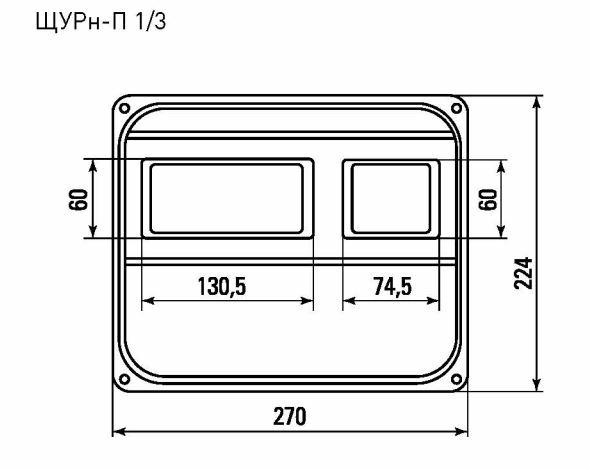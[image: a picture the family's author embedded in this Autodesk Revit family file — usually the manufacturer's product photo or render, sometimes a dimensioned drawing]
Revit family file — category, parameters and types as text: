
# Revit family: EKF_EE_ЩУРн_IP31_PROxima
name_source: partatom
category: Электрооборудование
units: mm (PartAtom-declared; Revit-internal decimal feet)

## family parameters
Всегда вертикально = Да
На основе рабочей плоскости = Нет
Общий = Нет
При загрузке вырезать с полостями = Нет
Размер круглого соединителя = Использовать диаметр
Тип детали = Силовой щит
Точка расчета площади = Да

## types (20) — shared parameters
ADSK_Единица измерения = компл.
ADSK_Завод-изготовитель = EKF
ADSK_Классификация нагрузок = Прочее
ADSK_Количество = 1
ADSK_Количество фаз = 3
ADSK_Коэффициент мощности = 1
ADSK_Материал = RAL 7035_Сталь
ADSK_Напряжение = 400 В
ADSK_Номинальная мощность = 0 Вт
ADSK_Полная мощность = 0 В·А
ADSK_Ток = 125 А
Изготовитель = EKF
Количество DIN-реек = 1
Серия номенклатуры = PROxima
Степень защиты IP = IP31
ТВ = EKF
Тип установки = Навесной
zero-valued in all types: Максимальное количество модулей

## per-type parameters (varying)
| type | ADSK_Код изделия | ADSK_Марка | ADSK_Масса | ADSK_Наименование | ADSK_Обозначение | ADSK_Размер_Высота | ADSK_Размер_Глубина | ADSK_Размер_Ширина | Количество модулей на DIN-рейке | Описание | Тип |
| ЩУРн 1/9 (400х300х140) IP31 EKF PROxima | mb23-1/9 | ЩУРн 1/9 IP31 | 4.38 | Щит учетно-распред. навесной ЩУРн 1/9 (400х300х140) IP31 EKF PROxima | ЩУРн 1/9 IP31 | 400 мм | 140 мм | 300 мм | 9 | Щит учетно-распред. навесной ЩУРн 1/9 (400х300х140) IP31 EKF PROxima | 17 мм |
| ЩУРн 1/12 (400x300x140) IP31 EKF PROxima | mb23-1/12 | ЩУРн 1/12 IP31 | 4.38 | Щит учетно-распред. навесной ЩУРн 1/12 (400x300x140) IP31 EKF PROxima | ЩУРн 1/12 IP31 | 400 мм | 140 мм | 300 мм | 12 | Щит учетно-распред. навесной ЩУРн 1/12 (400x300x140) IP31 EKF PROxima | 19 мм |
| ЩУРн 1/12 с шинами (400x300x140) IP31 EKF PROxima | mb23-1/12sh | ЩУРн 1/12 с шинами IP31 | 4.38 | Щит учетно-распред. навесной ЩУРн 1/12 с шинами (400x300x140) IP31 EKF PROxima | ЩУРн 1/12 с шинами IP31 | 400 мм | 140 мм | 300 мм | 12 | Щит учетно-распред. навесной ЩУРн 1/12 с шинами (400x300x140) IP31 EKF PROxima | 20 мм |
| ЩУРн 1/15 (400x360x140) IP31 EKF PROxima | mb23-1/15 | ЩУРн 1/15 IP31 | 5.6 | Щит учетно-распред. навесной ЩУРн 1/15 (400x360x140) IP31 EKF PROxima | ЩУРн 1/15 IP31 | 400 мм | 140 мм | 360 мм | 15 | Щит учетно-распред. навесной ЩУРн 1/15 (400x360x140) IP31 EKF PROxima | 21 мм |
| ЩУРн 3/12 (500х300х160) IP31 EKF PROxima | mb23-3/12 | ЩУРн 3/12 IP31 | 5.88 | Щит учетно-распред. навесной ЩУРн 3/12 (500х300х160) IP31 EKF PROxima | ЩУРн 3/12 IP31 | 500 мм | 160 мм | 300 мм | 12 | Щит учетно-распред. навесной ЩУРн 3/12 (500х300х160) IP31 EKF PROxima | 23 мм |
| ЩУРн 3/12 (Э) (500х300х120) IP31 EKF PROxima | mb23-3/12e | ЩУРн 3/12 (Э) IP31 | 5 | Щит учетно-распред. навесной счетчик на дин-рейку ЩУРн 3/12 (Э) (500х300х120) IP31 EKF PROxima | ЩУРн 3/12 (Э) IP31 | 500 мм | 120 мм | 300 мм | 12 | Щит учетно-распред. навесной счетчик на дин-рейку ЩУРн 3/12 (Э) (500х300х120) IP31 EKF PROxima | 24 мм |
| ЩУРн 3/18 (500х400х160) IP31 EKF PROxima | mb23-3/18 | ЩУРн 3/18 IP31 | 7 | Щит учетно-распред. навесной ЩУРн 3/18 (500х400х160) IP31 EKF PROxima | ЩУРн 3/18 IP31 | 500 мм | 160 мм | 400 мм | 18 | Щит учетно-распред. навесной ЩУРн 3/18 (500х400х160) IP31 EKF PROxima | 25 мм |
| ЩУРн 3/18 (Э) (500х340х120) IP31 EKF PROxima | mb23-3/18e | ЩУРн 3/18 (Э) IP31 | 5.2 | Щит учетно-распред. навесной счетчик на дин-рейку ЩУРн 3/18 (Э) (500х340х120) IP31 EKF PROxima | ЩУРн 3/18 (Э) IP31 | 500 мм | 120 мм | 340 мм | 18 | Щит учетно-распред. навесной счетчик на дин-рейку ЩУРн 3/18 (Э) (500х340х120) IP31 EKF PROxima | 26 мм |
| ЩУРн 3/24 (500х400х160) IP31 EKF PROxima | mb23-3/24 | ЩУРн 3/24 IP31 | 7.5 | Щит учетно-распред. навесной ЩУРн 3/24 (500х400х160) IP31 EKF PROxima | ЩУРн 3/24 IP31 | 500 мм | 160 мм | 400 мм | 24 | Щит учетно-распред. навесной ЩУРн 3/24 (500х400х160) IP31 EKF PROxima | 28 мм |
| ЩУРн 3/24 (Э) (500х400х120) IP31 EKF PROxima | mb23-3/24e | ЩУРн 3/24 (Э) IP31 | 5.4 | Щит учетно-распред. навесной счетчик на дин-рейку ЩУРн 3/24 (Э) (500х400х120) IP31 EKF PROxima | ЩУРн 3/24 (Э) IP31 | 500 мм | 120 мм | 400 мм | 24 | Щит учетно-распред. навесной счетчик на дин-рейку ЩУРн 3/24 (Э) (500х400х120) IP31 EKF PROxima | 29 мм |
| ЩУРн 3/30 (500х400х160) IP31 EKF PROxima | mb23-3/30-1 | ЩУРн 3/30 IP31 | 7.5 | Щит учетно-распред. навесной ЩУРн 3/30 (500х400х160) IP31 EKF PROxima | ЩУРн 3/30 IP31 | 500 мм | 160 мм | 400 мм | 30 | Щит учетно-распред. навесной ЩУРн 3/30 (500х400х160) IP31 EKF PROxima | 30 мм |
| ЩУРн 3/30 двухдверный (580х490х165) IP31 EKF PROxima | mb23-3/30-2 | ЩУРн 3/30 двухдверный IP31 | 10.75 | Щит учетно-распред. навесной ЩУРн 3/30 двухдверный (580х490х165) IP31 EKF PROxima | ЩУРн 3/30 двухдверный IP31 | 580 мм | 165 мм | 490 мм | 30 | Щит учетно-распред. навесной ЩУРн 3/30 двухдверный (580х490х165) IP31 EKF PROxima | 31 мм |
| ЩУРн 3/36 (560x550x165) IP31 EKF PROxima | mb23-3/36 | ЩУРн 3/36 IP31 | 9.8 | Щит учетно-распред. навесной ЩУРн 3/36 (560x550x165) IP31 EKF PROxima | ЩУРн 3/36 IP31 | 560 мм | 165 мм | 550 мм | 36 | Щит учетно-распред. навесной ЩУРн 3/36 (560x550x165) IP31 EKF PROxima | 32 мм |
| ЩУРн 3/48 (630х400х160) IP31 EKF PROxima | mb23-3/48 | ЩУРн 3/48 IP31 | 9.33 | Щит учетно-распред. навесной ЩУРн 3/48 (630х400х160) IP31 EKF PROxima | ЩУРн 3/48 IP31 | 630 мм | 160 мм | 400 мм | 48 | Щит учетно-распред. навесной ЩУРн 3/48 (630х400х160) IP31 EKF PROxima | 33 мм |
| ЩУРн 3/48 двухдверный (580х620х165) IP31 EKF PROxima | mb23-3/48-2 | ЩУРн 3/48 двухдверный IP31 | 13.12 | Щит учетно-распред. навесной ЩУРн 3/48 двухдверный (580х620х165) IP31 EKF PROxima | ЩУРн 3/48 двухдверный IP31 | 580 мм | 165 мм | 620 мм | 48 | Щит учетно-распред. навесной ЩУРн 3/48 двухдверный (580х620х165) IP31 EKF PROxima | 34 мм |
| ЩУРн 3/9 (500х300х160) IP31 EKF PROxima | mb23-3/9 | ЩУРн 3/9 IP31 | 5.88 | Щит учетно-распред. навесной ЩУРн 3/9 (500х300х160) IP31 EKF PROxima | ЩУРн 3/9 IP31 | 500 мм | 160 мм | 300 мм | 9 | Щит учетно-распред. навесной ЩУРн 3/9 (500х300х160) IP31 EKF PROxima | 35 мм |
| ЩУРн 3/9 (Э) (500х300х120) IP31 EKF PROxima | mb23-3/9e | ЩУРн 3/9 (Э) IP31 | 5 | Щит учетно-распред. навесной счетчик на дин-рейку ЩУРн 3/9 (Э) (500х300х120) IP31 EKF PROxima | ЩУРн 3/9 (Э) IP31 | 500 мм | 120 мм | 300 мм | 9 | Щит учетно-распред. навесной счетчик на дин-рейку ЩУРн 3/9 (Э) (500х300х120) IP31 EKF PROxima | 36 мм |
| ЩУРн 1/9 (Э) (360x280x110) IP31 EKF PROxima | mb23-1/9e | ЩУРн 1/9 (Э) IP31 | 3.5 | Щит учетно-распред. навесной счетчик на дин-рейку ЩУРн 1/9 (Э) (360x280x110) IP31 EKF PROxima | ЩУРн 1/9 (Э) IP31 | 360 мм | 110 мм | 280 мм | 9 | Щит учетно-распред. навесной счетчик на дин-рейку ЩУРн 1/9 (Э) (360x280x110) IP31 EKF PROxima | 38 мм |
| ЩУРн 1/12 (Э) (360х280х110) IP31 EKF PROxima | mb23-1/12e | ЩУРн 1/12 (Э) IP31 | 3.5 | Щит учетно-распред. навесной счетчик на дин-рейку ЩУРн 1/12 (Э) (360х280х110) IP31 EKF PROxima | ЩУРн 1/12 (Э) IP31 | 360 мм | 110 мм | 280 мм | 12 | Щит учетно-распред. навесной счетчик на дин-рейку ЩУРн 1/12 (Э) (360х280х110) IP31 EKF PROxima | 40 мм |
| ЩУРн- 1/6 (БУР) (300х150х135) IP31 EKF PROxima | mb23-1/6 | ЩУРн- 1/6 (БУР) IP31 | 0 | Щит учетно-распред. навесной ЩУРн- 1/6 (БУР) (300х150х135) IP31 EKF PROxima | ЩУРн- 1/6 (БУР) IP31 | 300 мм | 135 мм | 150 мм | 6 | Щит учетно-распред. навесной ЩУРн- 1/6 (БУР) (300х150х135) IP31 EKF PROxima | 41 мм |
